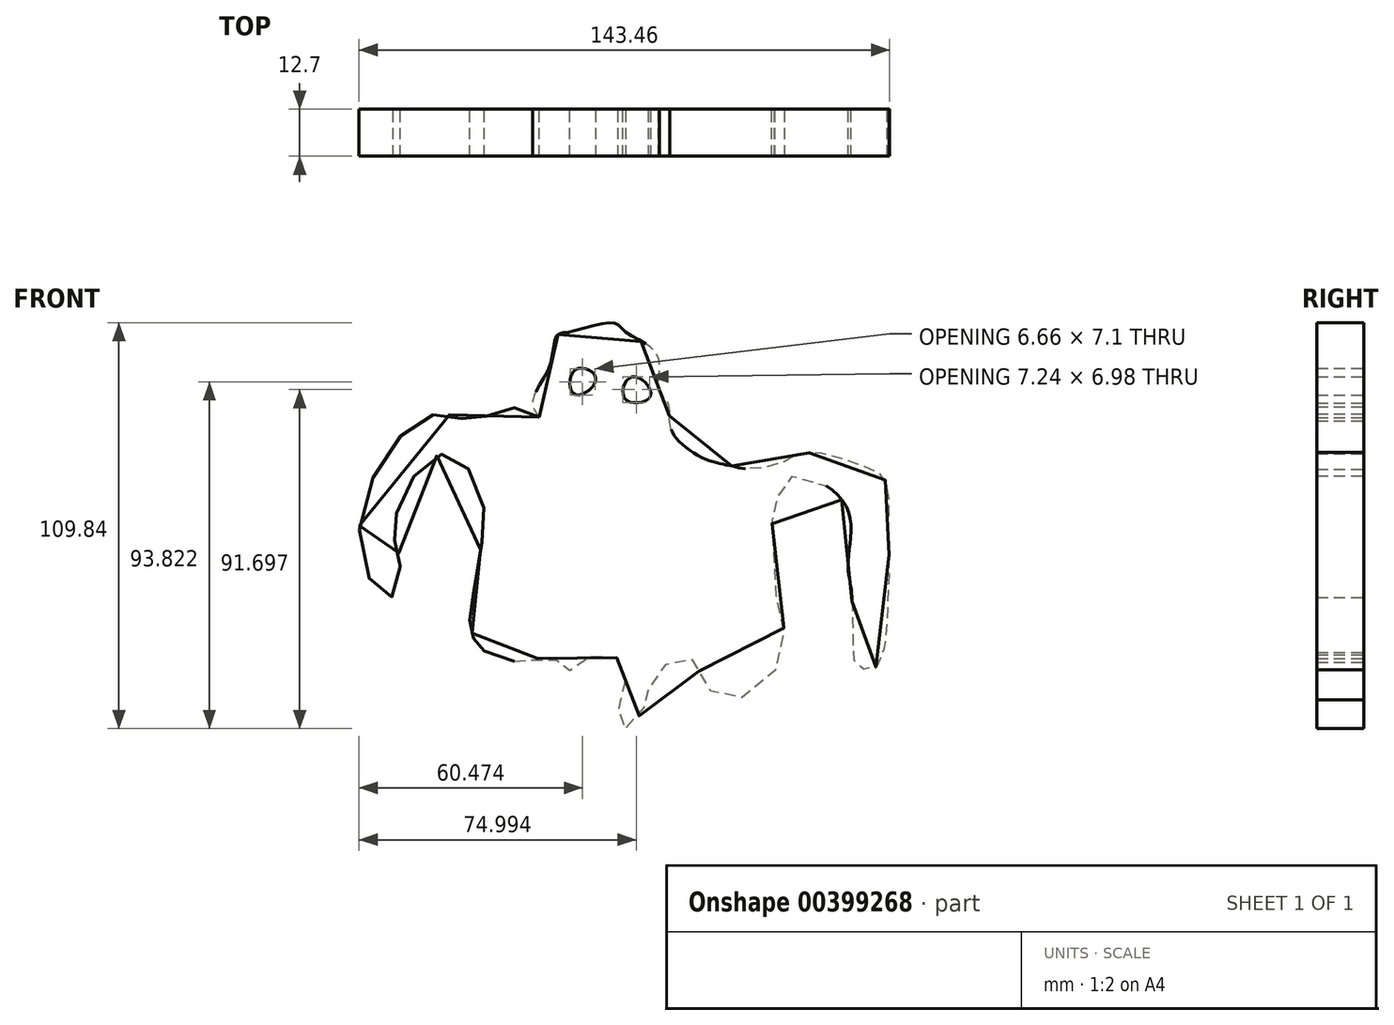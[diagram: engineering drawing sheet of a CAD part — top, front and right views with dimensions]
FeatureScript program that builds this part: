
annotation { "Feature Type Name" : "Feature", "Feature Type Description" : "" }
export const myFeature = defineFeature(function(context is Context, id is Id, definition is map)
    precondition{}
    {
        {
            var Q0;
            Q0=qCreatedBy(makeId("Front.planeOp"),FACE);
            var sketch = newSketch(context, id + "F0", { "sketchPlane" : qUnion([Q0])});
            skFitSpline(sketch, "E0", {"points": [v(-23.32, 46.07) * mm, v(-31.85, 48.92) * mm, v(-40.38, 45.12) * mm, v(-48.92, 47.02) * mm, v(-62.76, 38.68) * mm, v(-71.48, 8.72) * mm, v(-63.14, -2.46) * mm, v(-61.24, 9.67) * mm, v(-62.76, 14.6) * mm, v(-57.64, 29.39) * mm, v(-47.02, 36.02) * mm, v(-38.3, 21.61) * mm, v(-39.25, 9.86) * mm, v(-39.82, 5.88) * mm, v(-41.9, -7.02) * mm, v(-41.9, -10.05) * mm, v(-40.57, -14.79) * mm, v(-38.49, -16.87) * mm, v(-28.44, -20.1) * mm, v(-25.79, -19.53) * mm, v(-17.25, -20.1) * mm, v(-14.98, -22.37) * mm, v(-7.58, -17.63) * mm, v(0, -22) * mm, v(-1.9, -32.61) * mm, v(0, -38.1) * mm, v(6.26, -29.77) * mm, v(6.45, -26.92) * mm, v(16.12, -18.2) * mm, v(25.22, -29.77) * mm, v(42.1, -19.72) * mm, v(40.76, -1.52) * mm, v(40.38, 10.62) * mm, v(39.63, 16.5) * mm, v(40.57, 21.61) * mm, v(44.74, 29.96) * mm, v(59.53, 22.37) * mm, v(60.3, 7.2) * mm, v(61.05, 0) * mm, v(61.43, -5.69) * mm, v(61.62, -16.87) * mm, v(62.57, -20.86) * mm, v(67.3, -21.8) * mm, v(70.15, -16.12) * mm, v(70.72, -11.76) * mm, v(71.29, 10.05) * mm, v(70.9, 11.19) * mm, v(71.29, 18.4) * mm, v(71.1, 25.97) * mm, v(69.96, 29.77) * mm, v(65.6, 32.42) * mm, v(53.85, 36.21) * mm, v(51.57, 36.4) * mm, v(47.4, 36.4) * mm, v(43.42, 34.32) * mm, v(34.5, 32.04) * mm, v(28.44, 32.99) * mm, v(22.37, 34.5) * mm, v(13.65, 40.57) * mm, v(11.94, 45.88) * mm, v(11.57, 50.05) * mm, v(9.1, 53.66) * mm, v(8.72, 62.76) * mm, v(0, 69.2) * mm, v(-3.22, 71.67) * mm, v(-15.17, 69.2) * mm, v(-18.58, 68.07) * mm, v(-20.67, 59.34) * mm, v(-25.03, 49.48) * mm, v(-23.32, 46.07) * mm]});
            skFitSpline(sketch, "E1", {"points": [v(-13.46, 58.96) * mm, v(-7.96, 56.5) * mm, v(-13.65, 52.33) * mm, v(-13.46, 58.96) * mm]});
            skFitSpline(sketch, "E2", {"points": [v(1.9, 57.07) * mm, v(6.83, 51.95) * mm, v(0, 51) * mm, v(1.9, 57.07) * mm]});
            skSolve(sketch);
        }
        {
            var Q0;
            Q0=makeQuery(id+"F0.imprint","IMPRINT",FACE,{"disambiguationData":[TD([[makeQuery(id+"F0.imprint","IMPRINT",EDGE,{"derivedFrom":sQuery(id+"F0.wireOp",EDGE,"E0")}),1.0]])]});
            extrude(context, id + "F1", {"entities" : qUnion([Q0]), "depth" : 12.7 * mm});
        }
    });
